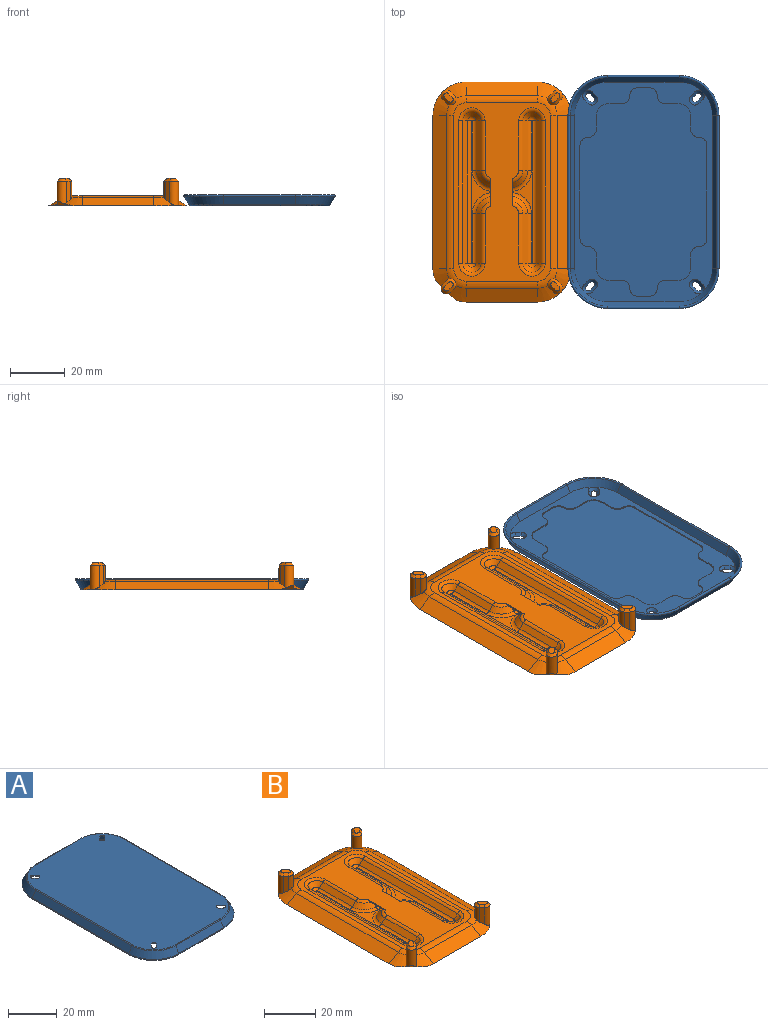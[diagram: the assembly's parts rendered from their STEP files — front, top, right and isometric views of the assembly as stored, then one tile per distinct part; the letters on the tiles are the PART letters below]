
ASSEMBLY  parts=2 mates=1
PART A: 83 faces, bbox 57.7x87.7x4 mm
  f0: plane 80.74x50.74mm, normal (0,0,1), area 3936.7mm2, adj f2,f3,f4,f5,f6,f7,f8,f9
  f1: plane 80.47x50.47mm, normal (0,0,-1), area 1043.7mm2, adj f2,f3,f4,f5,f6,f7,f8,f9
  f2: cone r=2mm half-angle=45deg, axis (0,0,-1), area 6.7mm2, adj f0,f1,f3,f4
  f3: plane 2.12x2.12mm, normal (-0.5,-0.5,-0.71), area 2.8mm2, adj f0,f1,f2,f5
  f4: plane 2.12x2.12mm, normal (0.5,0.5,-0.71), area 2.8mm2, adj f0,f1,f2,f5
  f5: cone r=2mm half-angle=45deg, axis (0,0,-1), area 6.7mm2, adj f0,f1,f3,f4
  f6: cone r=1mm half-angle=45deg, axis (0,0,-1), area 6.7mm2, adj f0,f1,f7,f8
  f7: plane 2.12x2.12mm, normal (-0.5,0.5,-0.71), area 2.8mm2, adj f0,f1,f6,f9
  f8: plane 2.12x2.12mm, normal (0.5,-0.5,-0.71), area 2.8mm2, adj f0,f1,f6,f9
  f9: cone r=1mm half-angle=45deg, axis (0,0,-1), area 6.7mm2, adj f0,f1,f7,f8
  f10: cone r=1mm half-angle=45deg, axis (0,0,-1), area 6.7mm2, adj f0,f1,f11,f12
  f11: plane 2.12x2.12mm, normal (0.5,-0.5,-0.71), area 2.8mm2, adj f0,f1,f10,f13
  f12: plane 2.12x2.12mm, normal (-0.5,0.5,-0.71), area 2.8mm2, adj f0,f1,f10,f13
  f13: cone r=1mm half-angle=45deg, axis (0,0,-1), area 6.7mm2, adj f0,f1,f11,f12
  f14: cone r=2mm half-angle=45deg, axis (0,0,-1), area 6.7mm2, adj f0,f1,f15,f16
  f15: plane 2.12x2.12mm, normal (0.5,0.5,-0.71), area 2.8mm2, adj f0,f1,f14,f17
  f16: plane 2.12x2.12mm, normal (-0.5,-0.5,-0.71), area 2.8mm2, adj f0,f1,f14,f17
  f17: cone r=2mm half-angle=45deg, axis (0,0,-1), area 6.7mm2, adj f0,f1,f15,f16
  f18: cylinder r=0.43mm len=26mm, axis (1,0,0), area 35.4mm2, adj f19,f20,f23,f47
  f19: plane 26x2.78mm, normal (0,0.87,-0.5), area 83.6mm2, adj f1,f18,f22,f46
  f20: plane 26x3.1mm, normal (0,-0.87,0.5), area 93.1mm2, adj f18,f21,f24,f48
  f21: cylinder r=0.5mm len=26mm, axis (1,0,0), area 13.6mm2, adj f0,f20,f25,f49
  f22: cone r=12.24mm half-angle=30deg, axis (0,0,-1), area 65.8mm2, adj f1,f19,f23,f26
  f23: torus R=14.22mm, axis (0,0,-1), area 30.7mm2, adj f18,f22,f24,f27
  f24: cone r=14.59mm half-angle=30deg, axis (0,0,-1), area 77mm2, adj f20,f23,f25,f28
  f25: torus R=12.37mm, axis (0,0,-1), area 10.4mm2, adj f0,f21,f24,f29
  f26: plane 56x2.78mm, normal (0.87,0,-0.5), area 180mm2, adj f1,f22,f27,f30
  f27: cylinder r=0.43mm len=56mm, axis (0,1,0), area 76.2mm2, adj f23,f26,f28,f31
  f28: plane 56x3.1mm, normal (-0.87,0,0.5), area 200.5mm2, adj f24,f27,f29,f32
  f29: cylinder r=0.5mm len=56mm, axis (0,1,0), area 29.3mm2, adj f0,f25,f28,f33
  f30: cone r=12.24mm half-angle=30deg, axis (0,0,-1), area 65.8mm2, adj f1,f26,f31,f34
  f31: torus R=14.22mm, axis (0,0,-1), area 30.7mm2, adj f27,f30,f32,f35
  f32: cone r=14.59mm half-angle=30deg, axis (0,0,-1), area 77mm2, adj f28,f31,f33,f36
  f33: torus R=12.37mm, axis (0,0,-1), area 10.4mm2, adj f0,f29,f32,f37
  f34: plane 26x2.78mm, normal (0,-0.87,-0.5), area 83.6mm2, adj f1,f30,f35,f38
  f35: cylinder r=0.43mm len=26mm, axis (1,0,0), area 35.4mm2, adj f31,f34,f36,f39
  f36: plane 26x3.1mm, normal (0,0.87,0.5), area 93.1mm2, adj f32,f35,f37,f40
  f37: cylinder r=0.5mm len=26mm, axis (1,0,0), area 13.6mm2, adj f0,f33,f36,f41
  f38: cone r=12.24mm half-angle=30deg, axis (0,0,-1), area 65.8mm2, adj f1,f34,f39,f42
  f39: torus R=14.22mm, axis (0,0,-1), area 30.7mm2, adj f35,f38,f40,f43
  f40: cone r=14.59mm half-angle=30deg, axis (0,0,-1), area 77mm2, adj f36,f39,f41,f44
  f41: torus R=12.37mm, axis (0,0,-1), area 10.4mm2, adj f0,f37,f40,f45
  f42: plane 56x2.78mm, normal (-0.87,0,-0.5), area 180mm2, adj f1,f38,f43,f46
  f43: cylinder r=0.43mm len=56mm, axis (0,-1,0), area 76.2mm2, adj f39,f42,f44,f47
  f44: plane 56x3.1mm, normal (0.87,0,0.5), area 200.5mm2, adj f40,f43,f45,f48
  f45: cylinder r=0.5mm len=56mm, axis (0,-1,0), area 29.3mm2, adj f0,f41,f44,f49
  f46: cone r=12.24mm half-angle=30deg, axis (0,0,-1), area 65.8mm2, adj f1,f19,f42,f47
  f47: torus R=14.22mm, axis (0,0,-1), area 30.7mm2, adj f18,f43,f46,f48
  f48: cone r=14.59mm half-angle=30deg, axis (0,0,-1), area 77mm2, adj f20,f44,f47,f49
  f49: torus R=12.37mm, axis (0,0,-1), area 10.4mm2, adj f0,f21,f45,f48
  f50: plane 5x0.4mm, normal (1,0,0), area 2mm2, adj f1,f51,f81,f82
  f51: cylinder r=3mm len=3mm, axis (0,0,-1), area 1.9mm2, adj f1,f50,f52,f82
  f52: cylinder r=3mm len=3mm, axis (0,0,-1), area 1.9mm2, adj f1,f51,f53,f82
  f53: plane 34x0.4mm, normal (1,0,0), area 13.6mm2, adj f1,f52,f54,f82
  f54: cylinder r=3mm len=3mm, axis (0,0,-1), area 1.9mm2, adj f1,f53,f55,f82
  f55: cylinder r=3mm len=3mm, axis (0,0,-1), area 1.9mm2, adj f1,f54,f56,f82
  f56: plane 5x0.4mm, normal (1,0,0), area 2mm2, adj f1,f55,f57,f82
  f57: cylinder r=4.24mm len=4.24mm, axis (0,0,-1), area 2.7mm2, adj f1,f56,f58,f82
  f58: plane 5x0.4mm, normal (0,-1,0), area 2mm2, adj f1,f57,f59,f82
  f59: cylinder r=3mm len=3mm, axis (0,0,-1), area 1.9mm2, adj f1,f58,f60,f82
  f60: cylinder r=3mm len=3mm, axis (0,0,-1), area 1.9mm2, adj f1,f59,f61,f82
  f61: plane 4x0.4mm, normal (0,-1,0), area 1.6mm2, adj f1,f60,f62,f82
  f62: cylinder r=3mm len=3mm, axis (0,0,-1), area 1.9mm2, adj f1,f61,f63,f82
  f63: cylinder r=3mm len=3mm, axis (0,0,-1), area 1.9mm2, adj f1,f62,f64,f82
  f64: plane 5x0.4mm, normal (0,-1,0), area 2mm2, adj f1,f63,f65,f82
  f65: cylinder r=4.24mm len=4.24mm, axis (0,0,-1), area 2.7mm2, adj f1,f64,f66,f82
  f66: plane 5x0.4mm, normal (-1,0,0), area 2mm2, adj f1,f65,f67,f82
  f67: cylinder r=3mm len=3mm, axis (0,0,-1), area 1.9mm2, adj f1,f66,f68,f82
  f68: cylinder r=3mm len=3mm, axis (0,0,-1), area 1.9mm2, adj f1,f67,f69,f82
  f69: plane 34x0.4mm, normal (-1,0,0), area 13.6mm2, adj f1,f68,f70,f82
  f70: cylinder r=3mm len=3mm, axis (0,0,-1), area 1.9mm2, adj f1,f69,f71,f82
  f71: cylinder r=3mm len=3mm, axis (0,0,-1), area 1.9mm2, adj f1,f70,f72,f82
  f72: plane 5x0.4mm, normal (-1,0,0), area 2mm2, adj f1,f71,f73,f82
  f73: cylinder r=4.24mm len=4.24mm, axis (0,0,-1), area 2.7mm2, adj f1,f72,f74,f82
  f74: plane 5x0.4mm, normal (0,1,0), area 2mm2, adj f1,f73,f75,f82
  f75: cylinder r=3mm len=3mm, axis (0,0,-1), area 1.9mm2, adj f1,f74,f76,f82
  f76: cylinder r=3mm len=3mm, axis (0,0,-1), area 1.9mm2, adj f1,f75,f77,f82
  f77: plane 4x0.4mm, normal (0,1,0), area 1.6mm2, adj f1,f76,f78,f82
  f78: cylinder r=3mm len=3mm, axis (0,0,-1), area 1.9mm2, adj f1,f77,f79,f82
  f79: cylinder r=3mm len=3mm, axis (0,0,-1), area 1.9mm2, adj f1,f78,f80,f82
  f80: plane 5x0.4mm, normal (0,1,0), area 2mm2, adj f1,f79,f81,f82
  f81: cylinder r=4.24mm len=4.24mm, axis (0,0,-1), area 2.7mm2, adj f1,f50,f80,f82
  f82: plane 76.47x46.47mm, normal (0,0,-1), area 2807mm2, adj f50,f51,f52,f53,f54,f55,f56,f57
PART B: 109 faces, bbox 50.6x80.6x10.1 mm
  f0: cone r=6mm half-angle=60deg, axis (0,0,-1), area 30.9mm2, adj f2,f14,f15,f98,f99,f105,f108
  f1: cone r=6mm half-angle=60deg, axis (0,0,-1), area 30.9mm2, adj f2,f15,f71,f97,f98,f105,f108
  f2: cylinder r=2mm len=8.5mm, axis (0,0,-1), area 50.1mm2, adj f0,f1,f97,f99,f101,f108
  f3: cone r=6mm half-angle=60deg, axis (0,0,-1), area 33.9mm2, adj f14,f15,f52,f53,f54,f61
  f4: cone r=6mm half-angle=60deg, axis (0,0,-1), area 33.9mm2, adj f13,f15,f39,f40,f42,f64
  f5: cone r=6mm half-angle=60deg, axis (0,0,-1), area 33.9mm2, adj f13,f15,f51,f52,f54,f61
  f6: cone r=4mm half-angle=45deg, axis (0,0,-1), area 22.3mm2, adj f7,f21,f28,f35,f48,f50
  f7: plane 6x1.81mm, normal (0,-0.71,0.71), area 15.4mm2, adj f6,f8,f27,f48
  f8: cone r=4mm half-angle=45deg, axis (0,0,-1), area 22.3mm2, adj f7,f9,f16,f26,f48,f49
  f9: torus R=3.17mm, axis (0,0,1), area 8mm2, adj f8,f10,f34,f49
  f10: plane 65.32x35.32mm, normal (0,0,1), area 1087.4mm2, adj f9,f32,f33,f34,f35,f36,f37,f38
  f11: plane 56x5.08mm, normal (0.5,0,0.87), area 328.2mm2, adj f12,f15,f62,f70
  f12: cone r=6mm half-angle=60deg, axis (0,0,-1), area 33.9mm2, adj f11,f15,f40,f41,f42,f64
  f13: plane 26x5.08mm, normal (0,0.5,0.87), area 152.4mm2, adj f4,f5,f15,f63
  f14: plane 56x5.08mm, normal (-0.5,0,0.87), area 328.2mm2, adj f0,f3,f15,f60
  f15: plane 80.47x50.47mm, normal (0,0,-1), area 3921mm2, adj f0,f1,f3,f4,f5,f11,f12,f13
  f16: plane 18x1.83mm, normal (-0.71,0,0.71), area 46.5mm2, adj f8,f17,f25,f34
  f17: cone r=4mm half-angle=45deg, axis (0,0,1), area 20.3mm2, adj f16,f18,f24,f33
  f18: plane 52x1.83mm, normal (0.71,0,0.71), area 134.5mm2, adj f17,f23,f32,f73
  f19: plane 52x1.83mm, normal (-0.71,0,0.71), area 134.5mm2, adj f20,f30,f38,f74
  f20: cone r=4mm half-angle=45deg, axis (0,0,1), area 20.3mm2, adj f19,f21,f31,f37
  f21: plane 18x1.83mm, normal (0.71,0,0.71), area 46.5mm2, adj f6,f20,f29,f36
  f22: plane 52.34x22.34mm, normal (0,0,1), area 95.9mm2, adj f23,f24,f25,f26,f27,f28,f29,f30
  f23: cylinder r=2mm len=52mm, axis (0,-1,0), area 81.7mm2, adj f18,f22,f24,f76
  f24: torus R=0.17mm, axis (0,0,1), area 4.5mm2, adj f17,f22,f23,f25
  f25: cylinder r=2mm len=18mm, axis (0,1,0), area 28.3mm2, adj f16,f22,f24,f26
  f26: torus R=7.83mm, axis (0,0,1), area 17.5mm2, adj f8,f22,f25,f27
  f27: cylinder r=2mm len=6mm, axis (-1,0,0), area 9.4mm2, adj f7,f22,f26,f28
  f28: torus R=7.83mm, axis (0,0,1), area 17.5mm2, adj f6,f22,f27,f29
  f29: cylinder r=2mm len=18mm, axis (0,-1,0), area 28.3mm2, adj f21,f22,f28,f31
  f30: cylinder r=2mm len=52mm, axis (0,1,0), area 81.7mm2, adj f19,f22,f31,f82
  f31: torus R=0.17mm, axis (0,0,1), area 4.5mm2, adj f20,f22,f29,f30
  f32: cylinder r=2mm len=52mm, axis (0,-1,0), area 81.7mm2, adj f10,f18,f33,f83
  f33: torus R=4.83mm, axis (0,0,1), area 20.1mm2, adj f10,f17,f32,f34
  f34: cylinder r=2mm len=18mm, axis (0,1,0), area 28.3mm2, adj f9,f10,f16,f33
  f35: torus R=3.17mm, axis (0,0,1), area 8mm2, adj f6,f10,f36,f50
  f36: cylinder r=2mm len=18mm, axis (0,-1,0), area 28.3mm2, adj f10,f21,f35,f37
  f37: torus R=4.83mm, axis (0,0,1), area 20.1mm2, adj f10,f20,f36,f38
  f38: cylinder r=2mm len=52mm, axis (0,1,0), area 81.7mm2, adj f10,f19,f37,f87
  f39: plane 8x1.46mm, normal (-0.71,0.71,0), area 14.8mm2, adj f4,f40,f42,f46
  f40: cylinder r=2mm len=9mm, axis (0,0,-1), area 54.2mm2, adj f4,f12,f39,f41,f44
  f41: plane 8x1.46mm, normal (0.71,-0.71,0), area 14.8mm2, adj f12,f40,f42,f45
  f42: cylinder r=2mm len=6.83mm, axis (0,0,-1), area 38.1mm2, adj f4,f12,f39,f41,f47,f64
  f43: plane 3.41x3.41mm, normal (0,0,1), area 7.1mm2, adj f44,f45,f46,f47
  f44: cone r=2mm half-angle=45deg, axis (0,0,-1), area 6.7mm2, adj f40,f43,f45,f46
  f45: plane 2.12x2.12mm, normal (0.5,-0.5,0.71), area 2.8mm2, adj f41,f43,f44,f47
  f46: plane 2.12x2.12mm, normal (-0.5,0.5,0.71), area 2.8mm2, adj f39,f43,f44,f47
  f47: cone r=2mm half-angle=45deg, axis (0,0,-1), area 6.7mm2, adj f42,f43,f45,f46
  f48: plane 8x7.02mm, normal (0,0,-1), area 54.5mm2, adj f6,f7,f8,f49,f50,f66,f67,f68
  f49: plane 10.09x0.7mm, normal (-1,0,0), area 4.8mm2, adj f8,f9,f10,f48,f68,f69
  f50: plane 10.09x0.7mm, normal (1,0,0), area 4.8mm2, adj f6,f10,f35,f48,f66,f85
  f51: plane 8x1.46mm, normal (0.71,0.71,0), area 14.8mm2, adj f5,f52,f54,f58
  f52: cylinder r=2mm len=6.83mm, axis (0,0,-1), area 38.1mm2, adj f3,f5,f51,f53,f59,f61
  f53: plane 8x1.46mm, normal (-0.71,-0.71,0), area 14.8mm2, adj f3,f52,f54,f57
  f54: cylinder r=2mm len=9mm, axis (0,0,-1), area 54.2mm2, adj f3,f5,f51,f53,f56
  f55: plane 3.41x3.41mm, normal (0,0,1), area 7.1mm2, adj f56,f57,f58,f59
  f56: cone r=1mm half-angle=45deg, axis (0,0,-1), area 6.7mm2, adj f54,f55,f57,f58
  f57: plane 2.12x2.12mm, normal (-0.5,-0.5,0.71), area 2.8mm2, adj f53,f55,f56,f59
  f58: plane 2.12x2.12mm, normal (0.5,0.5,0.71), area 2.8mm2, adj f51,f55,f56,f59
  f59: cone r=1mm half-angle=45deg, axis (0,0,-1), area 6.7mm2, adj f52,f55,f57,f58
  f60: cylinder r=5mm len=56mm, axis (0,1,0), area 146.6mm2, adj f10,f14,f61,f105
  f61: torus R=4.66mm, axis (0,0,1), area 22.2mm2, adj f3,f5,f10,f52,f60,f63
  f62: cylinder r=5mm len=56mm, axis (0,1,0), area 146.6mm2, adj f10,f11,f64,f107
  f63: cylinder r=5mm len=26mm, axis (1,0,0), area 68.1mm2, adj f10,f13,f61,f64
  f64: torus R=4.66mm, axis (0,0,1), area 22.2mm2, adj f4,f10,f12,f42,f62,f63
  f65: cone r=6mm half-angle=60deg, axis (0,0,-1), area 33.9mm2, adj f15,f71,f88,f89,f91,f107
  f66: cone r=4mm half-angle=45deg, axis (0,0,-1), area 22.3mm2, adj f48,f50,f67,f75,f80,f85
  f67: plane 6x1.81mm, normal (0,0.71,0.71), area 15.4mm2, adj f48,f66,f68,f79
  f68: cone r=4mm half-angle=45deg, axis (0,0,-1), area 22.3mm2, adj f48,f49,f67,f69,f72,f78
  f69: torus R=3.17mm, axis (0,0,1), area 8mm2, adj f10,f49,f68,f84
  f70: cone r=6mm half-angle=60deg, axis (0,0,-1), area 33.9mm2, adj f11,f15,f89,f90,f91,f107
  f71: plane 26x5.08mm, normal (0,-0.5,0.87), area 152.4mm2, adj f1,f15,f65,f106
  f72: plane 18x1.83mm, normal (-0.71,0,0.71), area 46.5mm2, adj f68,f73,f77,f84
  f73: cone r=4mm half-angle=45deg, axis (0,0,1), area 20.3mm2, adj f18,f72,f76,f83
  f74: cone r=4mm half-angle=45deg, axis (0,0,1), area 20.3mm2, adj f19,f75,f82,f87
  f75: plane 18x1.83mm, normal (0.71,0,0.71), area 46.5mm2, adj f66,f74,f81,f86
  f76: torus R=0.17mm, axis (0,0,1), area 4.5mm2, adj f22,f23,f73,f77
  f77: cylinder r=2mm len=18mm, axis (0,-1,0), area 28.3mm2, adj f22,f72,f76,f78
  f78: torus R=7.83mm, axis (0,0,1), area 17.5mm2, adj f22,f68,f77,f79
  f79: cylinder r=2mm len=6mm, axis (-1,0,0), area 9.4mm2, adj f22,f67,f78,f80
  f80: torus R=7.83mm, axis (0,0,1), area 17.5mm2, adj f22,f66,f79,f81
  f81: cylinder r=2mm len=18mm, axis (0,1,0), area 28.3mm2, adj f22,f75,f80,f82
  f82: torus R=0.17mm, axis (0,0,1), area 4.5mm2, adj f22,f30,f74,f81
  f83: torus R=4.83mm, axis (0,0,1), area 20.1mm2, adj f10,f32,f73,f84
  f84: cylinder r=2mm len=18mm, axis (0,-1,0), area 28.3mm2, adj f10,f69,f72,f83
  f85: torus R=3.17mm, axis (0,0,1), area 8mm2, adj f10,f50,f66,f86
  f86: cylinder r=2mm len=18mm, axis (0,1,0), area 28.3mm2, adj f10,f75,f85,f87
  f87: torus R=4.83mm, axis (0,0,1), area 20.1mm2, adj f10,f38,f74,f86
  f88: plane 8x1.46mm, normal (-0.71,-0.71,0), area 14.8mm2, adj f65,f89,f91,f95
  f89: cylinder r=2mm len=9mm, axis (0,0,-1), area 54.2mm2, adj f65,f70,f88,f90,f93
  f90: plane 8x1.46mm, normal (0.71,0.71,0), area 14.8mm2, adj f70,f89,f91,f94
  f91: cylinder r=2mm len=6.83mm, axis (0,0,-1), area 38.1mm2, adj f65,f70,f88,f90,f96,f107
  f92: plane 3.41x3.41mm, normal (0,0,1), area 7.1mm2, adj f93,f94,f95,f96
  f93: cone r=2mm half-angle=45deg, axis (0,0,-1), area 6.7mm2, adj f89,f92,f94,f95
  f94: plane 2.12x2.12mm, normal (0.5,0.5,0.71), area 2.8mm2, adj f90,f92,f93,f96
  f95: plane 2.12x2.12mm, normal (-0.5,-0.5,0.71), area 2.8mm2, adj f88,f92,f93,f96
  f96: cone r=2mm half-angle=45deg, axis (0,0,-1), area 6.7mm2, adj f91,f92,f94,f95
  f97: plane 8x1.46mm, normal (0.71,-0.71,0), area 14.8mm2, adj f1,f2,f98,f103
  f98: cylinder r=2mm len=6.83mm, axis (0,0,-1), area 38.1mm2, adj f0,f1,f97,f99,f104,f105
  f99: plane 8x1.46mm, normal (-0.71,0.71,0), area 14.8mm2, adj f0,f2,f98,f102
  f100: plane 3.41x3.41mm, normal (0,0,1), area 7.1mm2, adj f101,f102,f103,f104
  f101: cone r=1mm half-angle=45deg, axis (0,0,-1), area 6.7mm2, adj f2,f100,f102,f103
  f102: plane 2.12x2.12mm, normal (-0.5,0.5,0.71), area 2.8mm2, adj f99,f100,f101,f104
  f103: plane 2.12x2.12mm, normal (0.5,-0.5,0.71), area 2.8mm2, adj f97,f100,f101,f104
  f104: cone r=1mm half-angle=45deg, axis (0,0,-1), area 6.7mm2, adj f98,f100,f102,f103
  f105: torus R=4.66mm, axis (0,0,1), area 22.2mm2, adj f0,f1,f10,f60,f98,f106
  f106: cylinder r=5mm len=26mm, axis (1,0,0), area 68.1mm2, adj f10,f71,f105,f107
  f107: torus R=4.66mm, axis (0,0,1), area 22.2mm2, adj f10,f62,f65,f70,f91,f106
  f108: plane 8.3x8.3mm, normal (-0.5,-0.5,-0.71), area 9.4mm2, adj f0,f1,f2,f15
PLACE A rot(axis=(0,1,0),180deg) t=(62.14,2.58,23.72)mm
PLACE B t=(-19.64,2.58,9.92)mm
MATE planar A.f0 <-> B.f15  axis (0,0,-1) through (47.14,2.58,6.32)mm
